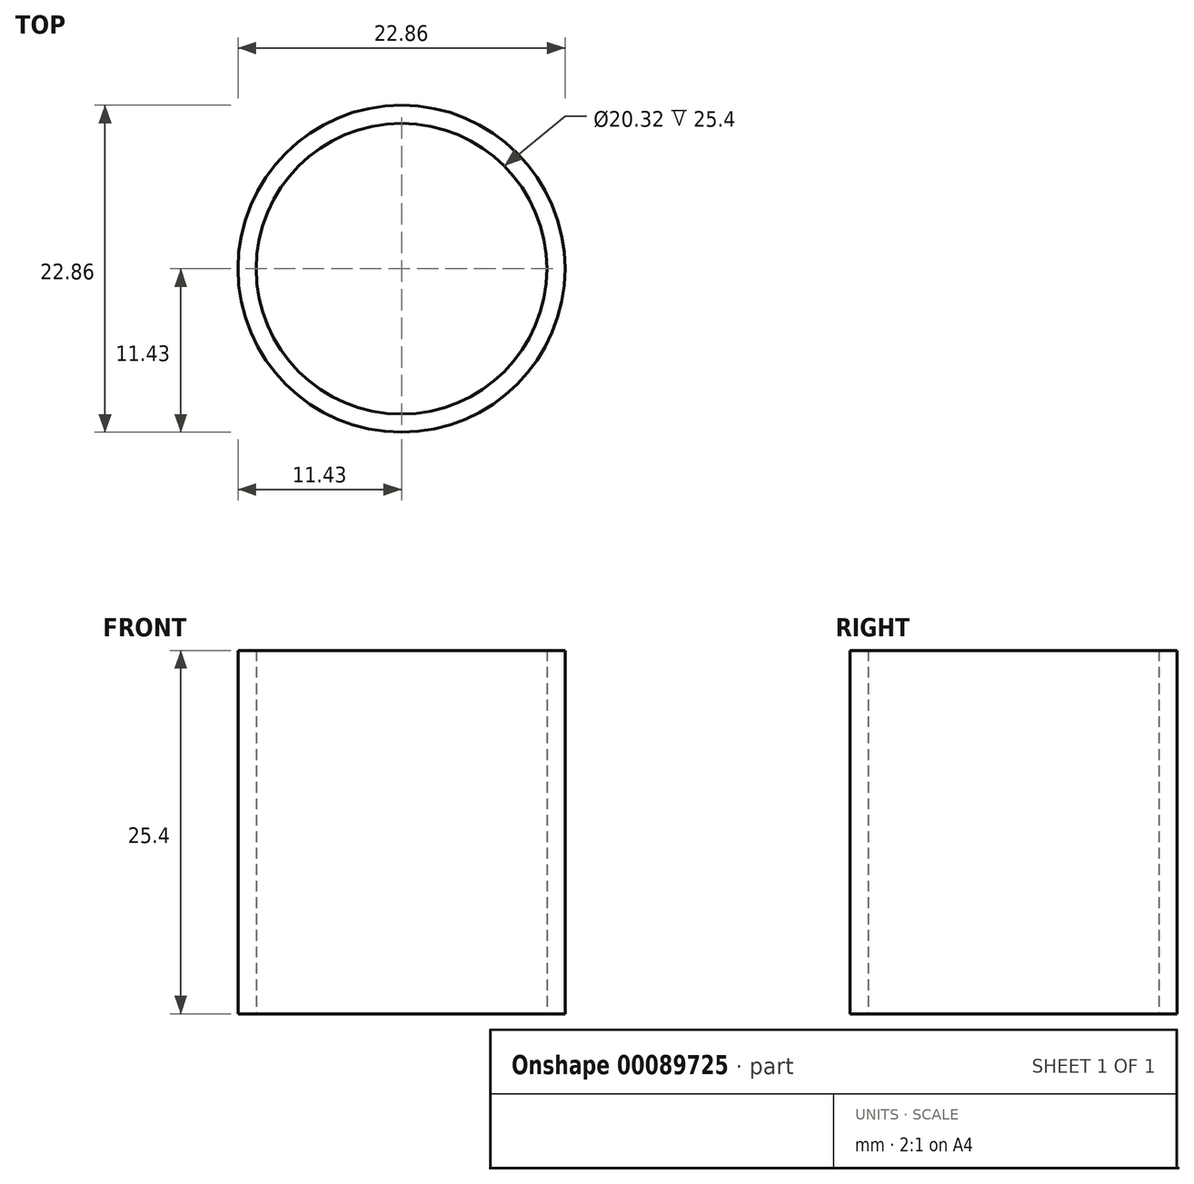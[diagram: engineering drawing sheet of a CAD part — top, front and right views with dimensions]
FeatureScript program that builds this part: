
annotation { "Feature Type Name" : "Feature", "Feature Type Description" : "" }
export const myFeature = defineFeature(function(context is Context, id is Id, definition is map)
    precondition{}
    {
        {
            var Q0;
            Q0=qCreatedBy(makeId("Top.planeOp"),FACE);
            var sketch = newSketch(context, id + "F0", { "sketchPlane" : qUnion([Q0])});
            skCircle(sketch, "E0", {"center": v(0, 0) * mm, "radius": 10.16 * mm});
            skCircle(sketch, "E1", {"center": v(0, 0) * mm, "radius": 11.43 * mm});
            skSolve(sketch);
        }
        {
            var Q0;
            Q0=makeQuery(id+"F0.imprint","IMPRINT",FACE,{"disambiguationData":[TD([[makeQuery(id+"F0.imprint","IMPRINT",EDGE,{"derivedFrom":sQuery(id+"F0.wireOp",EDGE,"E0")}),-1.0]])]});
            extrude(context, id + "F1", {"entities" : qUnion([Q0]), "depth" : 25.4 * mm});
        }
    });
